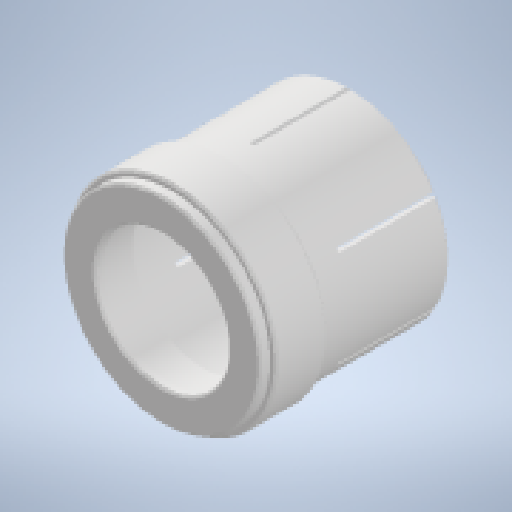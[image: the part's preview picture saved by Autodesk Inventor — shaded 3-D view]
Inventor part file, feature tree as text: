
AUTODESK INVENTOR PART (.ipt)
format: ipt  version: 2024 (Build 280153000, 153)  size: 364,032 bytes
history: native  units: mm
features: chamfer x2, pattern_circular x2, sketch x2, revolve x1, extrude x1, fillet x1
ambient origin geometry x8: Origin, YZ Plane, XZ Plane, XY Plane, X Axis, Y Axis, Z Axis, Center Point
bodies: Solid1 (feature_tree)
feature tree (9):
  revolve  "Revolution2"  [1 undecoded]
  chamfer  "Chamfer1"  Distance=21.3mm
  chamfer  "Chamfer2"  Distance=25.4mm
  extrude  "Extrusion1"  Depth=0.5mm
  pattern_circular  "Circular Pattern1"  [2 undecoded]
  fillet  "Fillet1"  Radius=2.0mm
  pattern_circular  "Circular Pattern2"  [2 undecoded]
  sketch  "Sketch2"  dims[d0=10.0mm d1=36.0mm]
  sketch  "Sketch4"  dims[d2=17.05mm d3=21.3mm d4=25.4mm d5=24.0mm d6=15.0mm d7=2.0mm d8=0.9mm d10=90.0deg d11=0.5mm d12=2.0mm d13=45.0deg d14=1.4mm d15=2.5mm d16=0.5mm d17=2.0mm d18=45.0deg d19=1.0mm d20=24.0mm d21=0.0mm d22=60.0mm d23=360.0deg d25=0.5mm d26=60.0mm d27=360.0deg]
note: 5 required parameter values undecoded (feature->parameter linkage not recoverable at this tier; creation-order binding heuristic only, values carry confidence <= 0.55)